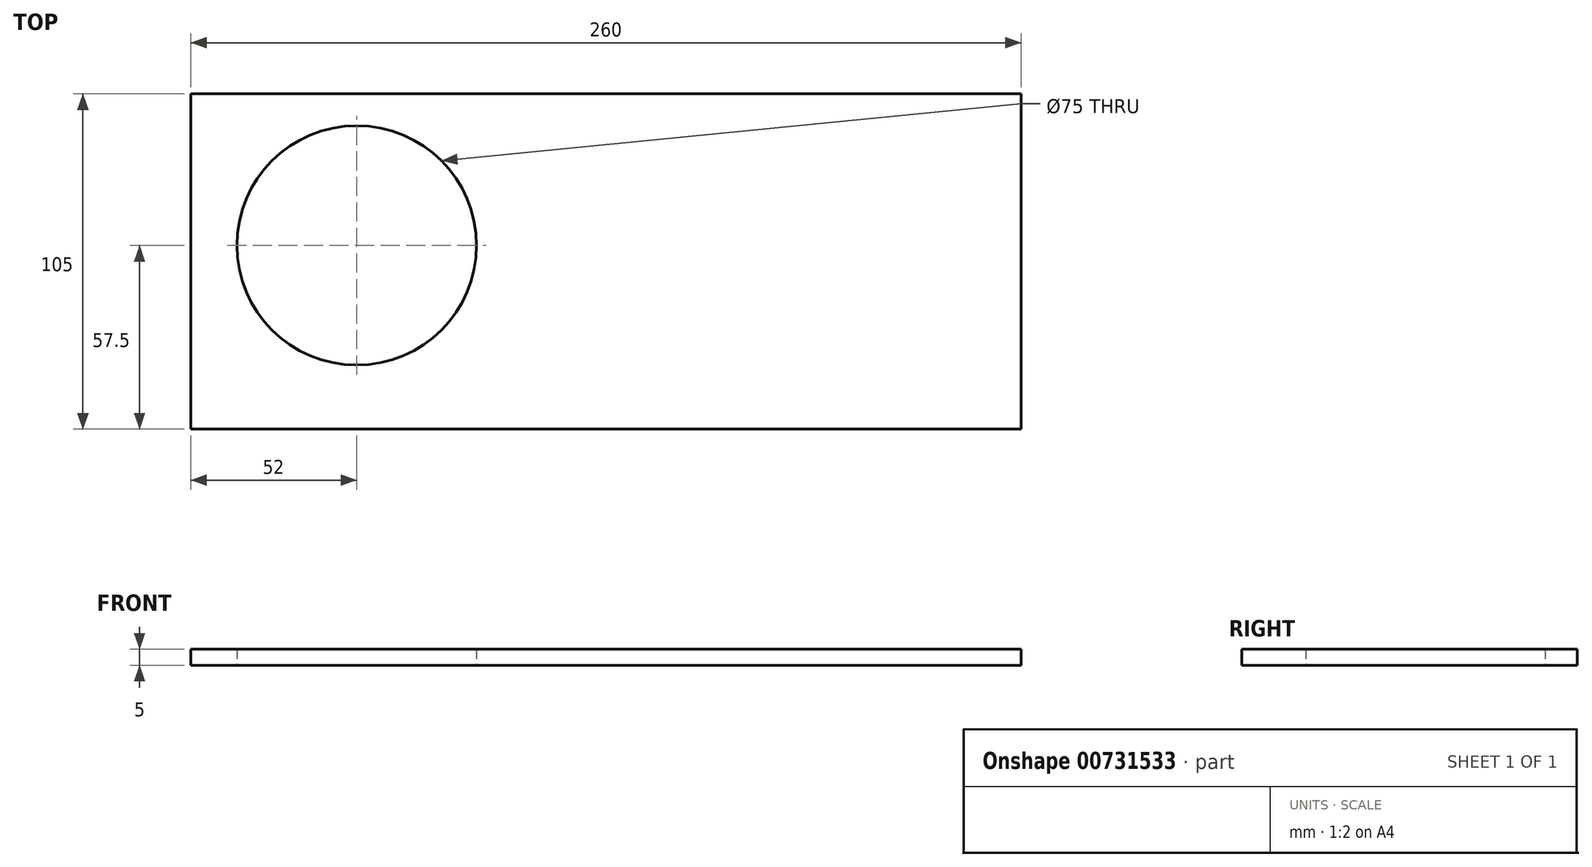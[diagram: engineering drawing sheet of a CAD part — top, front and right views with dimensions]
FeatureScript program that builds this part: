
annotation { "Feature Type Name" : "Feature", "Feature Type Description" : "" }
export const myFeature = defineFeature(function(context is Context, id is Id, definition is map)
    precondition{}
    {
        {
            var Q0;
            Q0=qCreatedBy(makeId("Top.planeOp"),FACE);
            var sketch = newSketch(context, id + "F0", { "sketchPlane" : qUnion([Q0])});
            skLineSegment(sketch, "E0.bottom", {"start": v(0, 0) * mm, "end": v(260, 0) * mm});
            skLineSegment(sketch, "E0.top", {"start": v(0, 105) * mm, "end": v(260, 105) * mm});
            skLineSegment(sketch, "E0.left", {"start": v(0, 0) * mm, "end": v(0, 105) * mm});
            skLineSegment(sketch, "E0.right", {"start": v(260, 0) * mm, "end": v(260, 105) * mm});
            skSolve(sketch);
        }
        {
            var Q0;
            Q0 = qSketchRegion(id + "F0", true);
            extrude(context, id + "F1", {"entities" : qUnion([Q0]), "depth" : 5 * mm, "offsetDistance" : 25 * mm});
        }
        {
            var Q0;
            Q0=qCreatedBy(makeId("Top.planeOp"),FACE);
            var sketch = newSketch(context, id + "F2", { "sketchPlane" : qUnion([Q0])});
            skCircle(sketch, "E1", {"center": v(52, 57.5) * mm, "radius": 37.5 * mm});
            skSolve(sketch);
        }
        {
            var Q0;
            Q0 = qSketchRegion(id + "F2", true);
            extrude(context, id + "F3", {"entities" : qUnion([Q0]), "operationType" : NewBodyOperationType.REMOVE, "endBound" : BoundingType.THROUGH_ALL, "depth" : 25 * mm, "offsetDistance" : 25 * mm});
        }
    });
